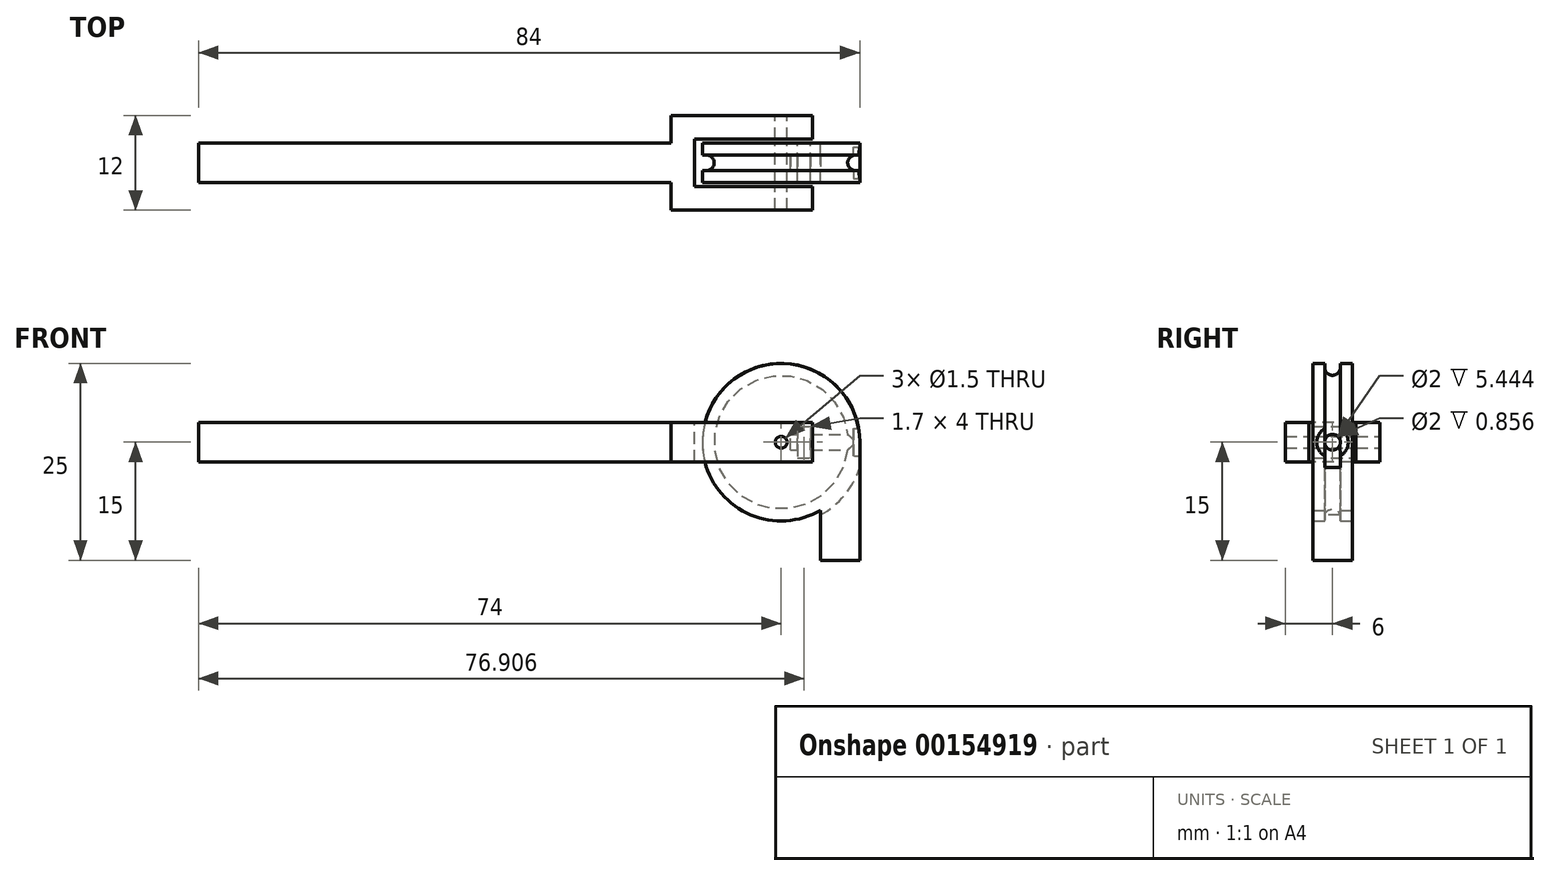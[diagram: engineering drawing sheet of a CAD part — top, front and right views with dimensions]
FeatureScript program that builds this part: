
annotation { "Feature Type Name" : "Feature", "Feature Type Description" : "" }
export const myFeature = defineFeature(function(context is Context, id is Id, definition is map)
    precondition{}
    {
        {
            var Q0;
            Q0=qCreatedBy(makeId("Front.planeOp"),FACE);
            var sketch = newSketch(context, id + "F0", { "sketchPlane" : qUnion([Q0])});
            skArc(sketch, "E0", {"start": v(10, 0) * mm, "mid": v(-8.66, 5) * mm, "end": v(5, -8.66) * mm});
            skLineSegment(sketch, "E1", {"start": v(10, 0) * mm, "end": v(10, -15) * mm});
            skLineSegment(sketch, "E2", {"start": v(10, -15) * mm, "end": v(5, -15) * mm});
            skLineSegment(sketch, "E3", {"start": v(5, -15) * mm, "end": v(5, -8.66) * mm});
            skCircle(sketch, "E4", {"center": v(0, 0) * mm, "radius": 0.75 * mm});
            skLineSegment(sketch, "E5.bottom", {"start": v(2.06, 2) * mm, "end": v(3.76, 2) * mm});
            skLineSegment(sketch, "E5.top", {"start": v(2.06, -2) * mm, "end": v(3.76, -2) * mm});
            skLineSegment(sketch, "E5.left", {"start": v(2.06, 2) * mm, "end": v(2.06, -2) * mm});
            skLineSegment(sketch, "E5.right", {"start": v(3.76, 2) * mm, "end": v(3.76, -2) * mm});
            skPoint(sketch, "E5.middle", {"position": v(2.9, 0) * mm});
            skSolve(sketch);
        }
        {
            var Q0;
            Q0=makeQuery(id+"F0.imprint","IMPRINT",FACE,{"disambiguationData":[TD([[makeQuery(id+"F0.imprint","IMPRINT",EDGE,{"derivedFrom":sQuery(id+"F0.wireOp",EDGE,"E0")}),1.0]])]});
            extrude(context, id + "F1", {"entities" : qUnion([Q0]), "depth" : 5 * mm});
        }
        {
            var Q0;
            Q0=makeQuery(id+"F1.opExtrude","SWEPT_FACE",FACE,{"disambiguationData":[OSD([sQuery(id+"F0.wireOp",EDGE,"E2")])]});
            var Q1;
            Q1=qCreatedBy(makeId("Origin.pointOp"),VERTEX);
            cPlane(context, id + "F2", {"entities" : qUnion([Q0, Q1]), "cplaneType" : CPlaneType.PLANE_POINT, "offset" : 25 * mm, "width" : 150 * mm, "height" : 150 * mm});
        }
        {
            var Q0;
            Q0=qCreatedBy(makeId("Right.planeOp"),FACE);
            var sketch = newSketch(context, id + "F3", { "sketchPlane" : qUnion([Q0])});
            skLineSegment(sketch, "E6", {"start": v(-5, 10) * mm, "end": v(-3.5, 10) * mm});
            skLineSegment(sketch, "E7.0", {"start": v(-5, -10) * mm, "end": v(-5, 10) * mm});
            skLineSegment(sketch, "E8.0", {"start": v(0, -10) * mm, "end": v(0, 10) * mm});
            skPoint(sketch, "E9.0", {"position": v(0, 0) * mm});
            skLineSegment(sketch, "E10.top", {"start": v(-1.5, 10.5) * mm, "end": v(-3.5, 10.5) * mm});
            skLineSegment(sketch, "E10.left", {"start": v(-1.5, 9.5) * mm, "end": v(-1.5, 10.5) * mm});
            skLineSegment(sketch, "E10.right", {"start": v(-3.5, 9.5) * mm, "end": v(-3.5, 10.5) * mm});
            skPoint(sketch, "E10.middle", {"position": v(-2.5, 10) * mm});
            skArc(sketch, "E11", {"start": v(-3.5, 9.5) * mm, "mid": v(-2.5, 8.5) * mm, "end": v(-1.5, 9.5) * mm});
            skLineSegment(sketch, "E12.trimOffspring", {"start": v(-1.5, 10) * mm, "end": v(0, 10) * mm});
            skLineSegment(sketch, "E13", {"start": v(0, 0) * mm, "end": v(-5, 0) * mm, "construction": true});
            skSolve(sketch);
        }
        {
            var Q0;
            {var subQ4=sQuery(id+"F3.wireOp",EDGE,"E10.top");Q0=makeQuery(id+"F3.imprint","IMPRINT",FACE,{"disambiguationData":[TD([[makeQuery(id+"F3.imprint","IMPRINT",EDGE,{"derivedFrom":subQ4}),1.0]])]});}
            var Q1;
            Q1=sQuery(id+"F3.wireOp",EDGE,"E13");
            revolve(context, id + "F4", {"operationType" : NewBodyOperationType.REMOVE, "entities" : qUnion([Q0]), "axis" : qUnion([Q1]), "revolveType" : RevolveType.FULL, "oppositeDirection" : true});
        }
        {
            var Q0;
            Q0=makeQuery(id+"F1.opExtrude","SWEPT_FACE",FACE,{"disambiguationData":[OSD([sQuery(id+"F0.wireOp",EDGE,"E1")])]});
            var sketch = newSketch(context, id + "F5", { "sketchPlane" : qUnion([Q0])});
            skLineSegment(sketch, "E14", {"start": v(-1.5, 0) * mm, "end": v(-3.5, 0) * mm, "construction": true});
            skPoint(sketch, "E15", {"position": v(-2.5, 0) * mm});
            skCircle(sketch, "E16", {"center": v(-2.5, 0) * mm, "radius": 2 * mm});
            skSolve(sketch);
        }
        {
            var Q0;
            {var subQ0=sQuery(id+"F5.wireOp",EDGE,"E16");var subQ2=sQuery(id+"F0.wireOp",EDGE,"E1");var subQ3=makeQuery(id+"F1.opExtrude","SWEPT_FACE",FACE,{"disambiguationData":[OSD([subQ2])]});var subQ4=makeQuery(id+"F4.opRevolve","SWEPT_FACE",FACE,{"disambiguationData":[OSD([sQuery(id+"F3.wireOp",EDGE,"E10.right")])]});var subQ7=makeQuery(id+"F4.boolean.opBoolean","INTERSECT",EDGE,{"derivedFrom":[subQ3,subQ4]});var subQ8=makeQuery(id+"F5.imprint","INTERSECT",VERTEX,{"derivedFrom":[subQ7,subQ0]});Q0=makeQuery(id+"F5.imprint","IMPRINT",FACE,{"disambiguationData":[TD([[makeQuery(id+"F5.imprint","IMPRINT",EDGE,{"disambiguationData":[TD([[subQ8,1.0]])],"derivedFrom":subQ0}),1.0]])]});}
            var Q1;
            {var subQ0=sQuery(id+"F5.wireOp",EDGE,"E16");var subQ2=sQuery(id+"F0.wireOp",EDGE,"E1");var subQ3=makeQuery(id+"F1.opExtrude","SWEPT_FACE",FACE,{"disambiguationData":[OSD([subQ2])]});var subQ4=makeQuery(id+"F4.opRevolve","SWEPT_FACE",FACE,{"disambiguationData":[OSD([sQuery(id+"F3.wireOp",EDGE,"E10.left")])]});var subQ7=makeQuery(id+"F4.boolean.opBoolean","INTERSECT",EDGE,{"derivedFrom":[subQ3,subQ4]});var subQ8=makeQuery(id+"F5.imprint","INTERSECT",VERTEX,{"derivedFrom":[subQ7,subQ0]});Q1=makeQuery(id+"F5.imprint","IMPRINT",FACE,{"disambiguationData":[TD([[makeQuery(id+"F5.imprint","IMPRINT",EDGE,{"disambiguationData":[TD([[subQ8,-1.0]])],"derivedFrom":subQ0}),1.0]])]});}
            var Q2;
            {var subQ5=sQuery(id+"F0.wireOp",EDGE,"E1");var subQ6=makeQuery(id+"F1.opExtrude","SWEPT_FACE",FACE,{"disambiguationData":[OSD([subQ5])]});var subQ7=makeQuery(id+"F4.opRevolve","SWEPT_FACE",FACE,{"disambiguationData":[OSD([sQuery(id+"F3.wireOp",EDGE,"E10.right")])]});var subQ10=makeQuery(id+"F4.boolean.opBoolean","INTERSECT",EDGE,{"derivedFrom":[subQ6,subQ7]});var subQ12=sQuery(id+"F5.wireOp",EDGE,"E16");var subQ13=makeQuery(id+"F5.imprint","INTERSECT",VERTEX,{"derivedFrom":[subQ10,subQ12]});Q2=makeQuery(id+"F5.imprint","IMPRINT",FACE,{"disambiguationData":[TD([[makeQuery(id+"F5.imprint","IMPRINT",EDGE,{"disambiguationData":[TD([[subQ13,-1.0]])],"derivedFrom":subQ12}),1.0]])]});}
            var Q3;
            Q3=makeQuery(id+"F4.boolean.opBoolean","COPY",FACE,{"derivedFrom":makeQuery(id+"F4.opRevolve","SWEPT_FACE",FACE,{"disambiguationData":[OSD([sQuery(id+"F3.wireOp",EDGE,"E11")])]})});
            extrude(context, id + "F6", {"entities" : qUnion([Q0, Q1, Q2]), "operationType" : NewBodyOperationType.REMOVE, "oppositeDirection" : true, "endBoundEntityFace" : qUnion([Q3]), "depth" : 0.8 * mm});
        }
        {
            var Q0;
            Q0=makeQuery(id+"F6.boolean.opBoolean","COPY",FACE,{"derivedFrom":makeQuery(id+"F6.opExtrude","CAP_FACE",FACE,{"disambiguationData":[OSD([sQuery(id+"F5.wireOp",EDGE,"E16")])],"isStart":false})});
            var sketch = newSketch(context, id + "F7", { "sketchPlane" : qUnion([Q0])});
            skLineSegment(sketch, "E17", {"start": v(-0.5, 0) * mm, "end": v(-0.5, 0) * mm});
            skPoint(sketch, "E18", {"position": v(-2.5, 0) * mm});
            skCircle(sketch, "E19", {"center": v(-2.5, 0) * mm, "radius": 1 * mm});
            skSolve(sketch);
        }
        {
            var Q0;
            Q0=makeQuery(id+"F7.imprint","IMPRINT",FACE,{"disambiguationData":[TD([[makeQuery(id+"F7.imprint","IMPRINT",EDGE,{"derivedFrom":sQuery(id+"F7.wireOp",EDGE,"E19")}),1.0]])]});
            extrude(context, id + "F8", {"entities" : qUnion([Q0]), "operationType" : NewBodyOperationType.REMOVE, "oppositeDirection" : true, "depth" : 8 * mm});
        }
        {
            var Q0;
            Q0=qCreatedBy(id+"F2.planeOp",FACE);
            var sketch = newSketch(context, id + "F9", { "sketchPlane" : qUnion([Q0])});
            skLineSegment(sketch, "E20.0", {"start": v(9.85, 1.5) * mm, "end": v(-10, 1.5) * mm});
            skLineSegment(sketch, "E21.0", {"start": v(9.85, 3.5) * mm, "end": v(-10, 3.5) * mm});
            skArc(sketch, "E22", {"start": v(-9.5, 1.5) * mm, "mid": v(-8.5, 2.5) * mm, "end": v(-9.5, 3.5) * mm});
            skFitSpline(sketch, "E23.0", {"points": [v(9.2, 1.54) * mm, v(9.11, 1.57) * mm, v(8.94, 1.65) * mm, v(8.7, 1.84) * mm, v(8.5, 2.12) * mm, v(8.41, 2.5) * mm, v(8.5, 2.88) * mm, v(8.7, 3.16) * mm, v(8.93, 3.35) * mm, v(9.11, 3.43) * mm, v(9.2, 3.46) * mm]});
            skLineSegment(sketch, "E24", {"start": v(-9.5, 2.5) * mm, "end": v(9.2, 2.5) * mm, "construction": true});
            skLineSegment(sketch, "E25", {"start": v(4, -0.5) * mm, "end": v(-11, -0.5) * mm});
            skLineSegment(sketch, "E26", {"start": v(-11, -0.5) * mm, "end": v(-11, 2.5) * mm});
            skLineSegment(sketch, "E27", {"start": v(-11, 2.5) * mm, "end": v(-74, 2.5) * mm});
            skLineSegment(sketch, "E28", {"start": v(-74, 2.5) * mm, "end": v(-74, 0) * mm});
            skLineSegment(sketch, "E29", {"start": v(-74, 0) * mm, "end": v(-14, 0) * mm});
            skLineSegment(sketch, "E30", {"start": v(-14, 0) * mm, "end": v(-14, -3.5) * mm});
            skLineSegment(sketch, "E31", {"start": v(-14, -3.5) * mm, "end": v(4, -3.5) * mm});
            skLineSegment(sketch, "E32", {"start": v(4, -3.5) * mm, "end": v(4, -0.5) * mm});
            skLineSegment(sketch, "E33.MirrorCS", {"start": v(-11, 5.5) * mm, "end": v(-11, 2.5) * mm});
            skLineSegment(sketch, "E34.MirrorCS", {"start": v(4, 5.5) * mm, "end": v(-11, 5.5) * mm});
            skLineSegment(sketch, "E35.MirrorCS", {"start": v(4, 8.5) * mm, "end": v(4, 5.5) * mm});
            skLineSegment(sketch, "E36.MirrorCS", {"start": v(-74, 5) * mm, "end": v(-14, 5) * mm});
            skLineSegment(sketch, "E37.MirrorCS", {"start": v(-74, 2.5) * mm, "end": v(-74, 5) * mm});
            skLineSegment(sketch, "E38.MirrorCS", {"start": v(-14, 5) * mm, "end": v(-14, 8.5) * mm});
            skLineSegment(sketch, "E39.MirrorCS", {"start": v(-14, 8.5) * mm, "end": v(4, 8.5) * mm});
            skLineSegment(sketch, "E40.0", {"start": v(-10, 0) * mm, "end": v(10, 0) * mm});
            skSolve(sketch);
        }
        {
            var Q0;
            Q0=makeQuery(id+"F9.imprint","IMPRINT",FACE,{"disambiguationData":[TD([[makeQuery(id+"F9.imprint","IMPRINT",EDGE,{"derivedFrom":sQuery(id+"F9.wireOp",EDGE,"E25")}),1.0]])]});
            var Q1;
            Q1=makeQuery(id+"F9.imprint","IMPRINT",FACE,{"disambiguationData":[TD([[makeQuery(id+"F9.imprint","IMPRINT",EDGE,{"derivedFrom":sQuery(id+"F9.wireOp",EDGE,"E27")}),-1.0]])]});
            extrude(context, id + "F10", {"entities" : qUnion([Q0, Q1]), "depth" : 2.5 * mm, "hasSecondDirection" : true, "secondDirectionOppositeDirection" : true, "secondDirectionDepth" : 2.5 * mm});
        }
        {
            var Q0;
            Q0=makeQuery(id+"F10.opExtrude","SWEPT_FACE",FACE,{"disambiguationData":[OSD([sQuery(id+"F9.wireOp",EDGE,"E31")])]});
            var sketch = newSketch(context, id + "F11", { "sketchPlane" : qUnion([Q0])});
            skCircle(sketch, "E41", {"center": v(0, 0) * mm, "radius": 0.75 * mm});
            skSolve(sketch);
        }
        {
            var Q0;
            Q0=makeQuery(id+"F11.imprint","IMPRINT",FACE,{"disambiguationData":[TD([[makeQuery(id+"F11.imprint","IMPRINT",EDGE,{"derivedFrom":sQuery(id+"F11.wireOp",EDGE,"E41")}),1.0]])]});
            var Q1;
            Q1=makeQuery(id+"F10.opExtrude","SWEPT_FACE",FACE,{"disambiguationData":[OSD([sQuery(id+"F9.wireOp",EDGE,"E39.MirrorCS")])]});
            extrude(context, id + "F12", {"entities" : qUnion([Q0]), "operationType" : NewBodyOperationType.REMOVE, "endBound" : BoundingType.UP_TO_SURFACE, "oppositeDirection" : true, "endBoundEntityFace" : qUnion([Q1]), "depth" : 25 * mm});
        }
    });
